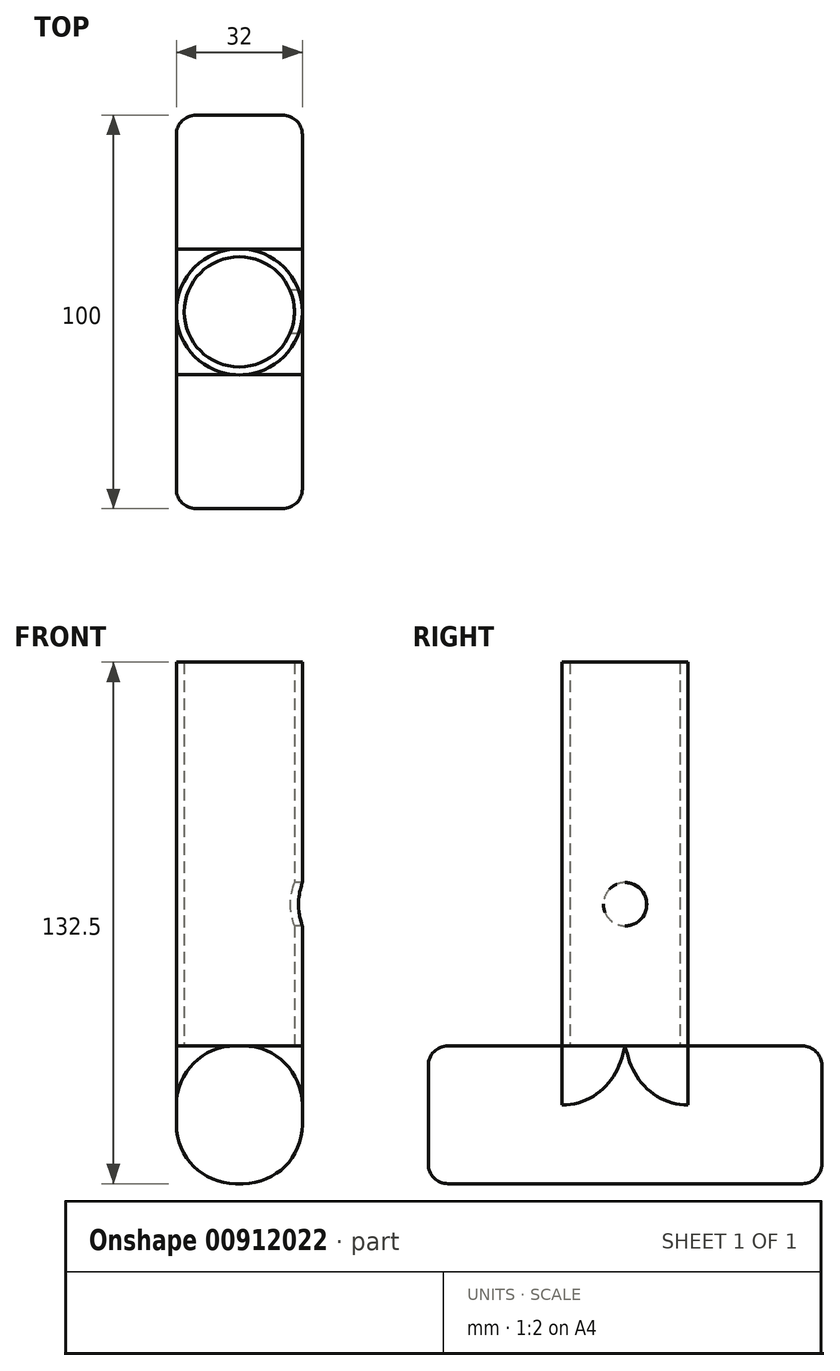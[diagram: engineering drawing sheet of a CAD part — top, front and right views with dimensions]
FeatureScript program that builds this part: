
annotation { "Feature Type Name" : "Feature", "Feature Type Description" : "" }
export const myFeature = defineFeature(function(context is Context, id is Id, definition is map)
    precondition{}
    {
        {
            var Q0;
            Q0=qCreatedBy(makeId("Top.planeOp"),FACE);
            var sketch = newSketch(context, id + "F0", { "sketchPlane" : qUnion([Q0])});
            skCircle(sketch, "E0", {"center": v(0, 0) * mm, "radius": 14 * mm});
            skCircle(sketch, "E1", {"center": v(0, 0) * mm, "radius": 16 * mm});
            skSolve(sketch);
        }
        {
            var Q0;
            Q0 = qSketchRegion(id + "F0", true);
            extrude(context, id + "F1", {"entities" : qUnion([Q0]), "depth" : 115 * mm, "offsetDistance" : 25 * mm});
        }
        {
            var Q0;
            Q0=qCreatedBy(makeId("Right.planeOp"),FACE);
            var sketch = newSketch(context, id + "F2", { "sketchPlane" : qUnion([Q0])});
            skCircle(sketch, "E2", {"center": v(0, 53.5) * mm, "radius": 5.5 * mm});
            skLineSegment(sketch, "E3", {"start": v(0, 0) * mm, "end": v(0, 104.05) * mm, "construction": true});
            skLineSegment(sketch, "E4", {"start": v(0, 115) * mm, "end": v(39.41, 115) * mm, "construction": true});
            skSolve(sketch);
        }
        {
            var Q0;
            Q0 = qSketchRegion(id + "F2", true);
            extrude(context, id + "F3", {"entities" : qUnion([Q0]), "operationType" : NewBodyOperationType.REMOVE, "endBound" : BoundingType.THROUGH_ALL, "depth" : 4 * mm, "offsetDistance" : 25 * mm});
        }
        {
            var Q0;
            Q0=qCreatedBy(makeId("Right.planeOp"),FACE);
            var sketch = newSketch(context, id + "F4", { "sketchPlane" : qUnion([Q0])});
            skLineSegment(sketch, "E5.bottom", {"start": v(50, 17.5) * mm, "end": v(-50, 17.5) * mm});
            skLineSegment(sketch, "E5.top", {"start": v(50, -17.5) * mm, "end": v(-50, -17.5) * mm});
            skLineSegment(sketch, "E5.left", {"start": v(50, 17.5) * mm, "end": v(50, -17.5) * mm});
            skLineSegment(sketch, "E5.right", {"start": v(-50, 17.5) * mm, "end": v(-50, -17.5) * mm});
            skPoint(sketch, "E5.middle", {"position": v(0, 0) * mm});
            skSolve(sketch);
        }
        {
            var Q0;
            Q0 = qSketchRegion(id + "F4", true);
            extrude(context, id + "F5", {"entities" : qUnion([Q0]), "operationType" : NewBodyOperationType.ADD, "depth" : 16 * mm, "offsetDistance" : 25 * mm, "hasSecondDirection" : true, "secondDirectionOppositeDirection" : true, "secondDirectionDepth" : 16 * mm});
        }
        {
            var Q0;
            Q0=makeQuery(id+"F5.opExtrude","CAP_EDGE",EDGE,{"disambiguationData":[OSD([sQuery(id+"F4.wireOp",EDGE,"E5.top")])],"isStart":true});
            var Q1;
            Q1=makeQuery(id+"F5.opExtrude","CAP_EDGE",EDGE,{"disambiguationData":[OSD([sQuery(id+"F4.wireOp",EDGE,"E5.top")])],"isStart":false});
            var Q2;
            Q2=makeQuery(id+"F5.opExtrude","CAP_EDGE",EDGE,{"disambiguationData":[OSD([sQuery(id+"F4.wireOp",EDGE,"E5.bottom")])],"isStart":true});
            var Q3;
            Q3=makeQuery(id+"F5.opExtrude","CAP_EDGE",EDGE,{"disambiguationData":[OSD([sQuery(id+"F4.wireOp",EDGE,"E5.bottom")])],"isStart":false});
            fillet(context, id + "F6", {"entities" : qUnion([Q0, Q1, Q2, Q3]), "radius" : 15 * mm, "tangentPropagation" : true, "allowEdgeOverflow" : false});
        }
        {
            var Q0;
            Q0=makeQuery(id+"F6.opFillet","BLEND_EDGE",EDGE,{"blendedFrom":[makeQuery(id+"F5.opExtrude","CAP_EDGE",EDGE,{"disambiguationData":[OSD([sQuery(id+"F4.wireOp",EDGE,"E5.top")])],"isStart":false}),makeQuery(id+"F5.opExtrude","SWEPT_FACE",FACE,{"disambiguationData":[OSD([sQuery(id+"F4.wireOp",EDGE,"E5.right")])]})],"blendedInto":[makeQuery(id+"F5.opExtrude","SWEPT_FACE",FACE,{"disambiguationData":[OSD([sQuery(id+"F4.wireOp",EDGE,"E5.right")])]})]});
            var Q1;
            Q1=makeQuery(id+"F6.opFillet","BLEND_EDGE",EDGE,{"blendedFrom":[makeQuery(id+"F5.opExtrude","CAP_EDGE",EDGE,{"disambiguationData":[OSD([sQuery(id+"F4.wireOp",EDGE,"E5.top")])],"isStart":true}),makeQuery(id+"F5.opExtrude","SWEPT_FACE",FACE,{"disambiguationData":[OSD([sQuery(id+"F4.wireOp",EDGE,"E5.right")])]})],"blendedInto":[makeQuery(id+"F5.opExtrude","SWEPT_FACE",FACE,{"disambiguationData":[OSD([sQuery(id+"F4.wireOp",EDGE,"E5.right")])]})]});
            var Q2;
            Q2=makeQuery(id+"F6.opFillet","BLEND_EDGE",EDGE,{"blendedFrom":[makeQuery(id+"F5.opExtrude","CAP_EDGE",EDGE,{"disambiguationData":[OSD([sQuery(id+"F4.wireOp",EDGE,"E5.bottom")])],"isStart":true}),makeQuery(id+"F5.opExtrude","SWEPT_FACE",FACE,{"disambiguationData":[OSD([sQuery(id+"F4.wireOp",EDGE,"E5.right")])]})],"blendedInto":[makeQuery(id+"F5.opExtrude","SWEPT_FACE",FACE,{"disambiguationData":[OSD([sQuery(id+"F4.wireOp",EDGE,"E5.right")])]})]});
            var Q3;
            Q3=makeQuery(id+"F6.opFillet","BLEND_EDGE",EDGE,{"blendedFrom":[makeQuery(id+"F5.opExtrude","CAP_EDGE",EDGE,{"disambiguationData":[OSD([sQuery(id+"F4.wireOp",EDGE,"E5.bottom")])],"isStart":false}),makeQuery(id+"F5.opExtrude","SWEPT_FACE",FACE,{"disambiguationData":[OSD([sQuery(id+"F4.wireOp",EDGE,"E5.right")])]})],"blendedInto":[makeQuery(id+"F5.opExtrude","SWEPT_FACE",FACE,{"disambiguationData":[OSD([sQuery(id+"F4.wireOp",EDGE,"E5.right")])]})]});
            var Q4;
            Q4=makeQuery(id+"F6.opFillet","BLEND_EDGE",EDGE,{"blendedFrom":[makeQuery(id+"F5.opExtrude","CAP_EDGE",EDGE,{"disambiguationData":[OSD([sQuery(id+"F4.wireOp",EDGE,"E5.top")])],"isStart":false}),makeQuery(id+"F5.opExtrude","SWEPT_FACE",FACE,{"disambiguationData":[OSD([sQuery(id+"F4.wireOp",EDGE,"E5.left")])]})],"blendedInto":[makeQuery(id+"F5.opExtrude","SWEPT_FACE",FACE,{"disambiguationData":[OSD([sQuery(id+"F4.wireOp",EDGE,"E5.left")])]})]});
            var Q5;
            Q5=makeQuery(id+"F6.opFillet","BLEND_EDGE",EDGE,{"blendedFrom":[makeQuery(id+"F5.opExtrude","CAP_EDGE",EDGE,{"disambiguationData":[OSD([sQuery(id+"F4.wireOp",EDGE,"E5.top")])],"isStart":true}),makeQuery(id+"F5.opExtrude","SWEPT_FACE",FACE,{"disambiguationData":[OSD([sQuery(id+"F4.wireOp",EDGE,"E5.left")])]})],"blendedInto":[makeQuery(id+"F5.opExtrude","SWEPT_FACE",FACE,{"disambiguationData":[OSD([sQuery(id+"F4.wireOp",EDGE,"E5.left")])]})]});
            var Q6;
            Q6=makeQuery(id+"F6.opFillet","BLEND_EDGE",EDGE,{"blendedFrom":[makeQuery(id+"F5.opExtrude","CAP_EDGE",EDGE,{"disambiguationData":[OSD([sQuery(id+"F4.wireOp",EDGE,"E5.bottom")])],"isStart":true}),makeQuery(id+"F5.opExtrude","SWEPT_FACE",FACE,{"disambiguationData":[OSD([sQuery(id+"F4.wireOp",EDGE,"E5.left")])]})],"blendedInto":[makeQuery(id+"F5.opExtrude","SWEPT_FACE",FACE,{"disambiguationData":[OSD([sQuery(id+"F4.wireOp",EDGE,"E5.left")])]})]});
            var Q7;
            Q7=makeQuery(id+"F6.opFillet","BLEND_EDGE",EDGE,{"blendedFrom":[makeQuery(id+"F5.opExtrude","CAP_EDGE",EDGE,{"disambiguationData":[OSD([sQuery(id+"F4.wireOp",EDGE,"E5.bottom")])],"isStart":false}),makeQuery(id+"F5.opExtrude","SWEPT_FACE",FACE,{"disambiguationData":[OSD([sQuery(id+"F4.wireOp",EDGE,"E5.left")])]})],"blendedInto":[makeQuery(id+"F5.opExtrude","SWEPT_FACE",FACE,{"disambiguationData":[OSD([sQuery(id+"F4.wireOp",EDGE,"E5.left")])]})]});
            fillet(context, id + "F7", {"entities" : qUnion([Q0, Q1, Q2, Q3, Q4, Q5, Q6, Q7]), "radius" : 5 * mm, "tangentPropagation" : true, "allowEdgeOverflow" : false});
        }
    });
